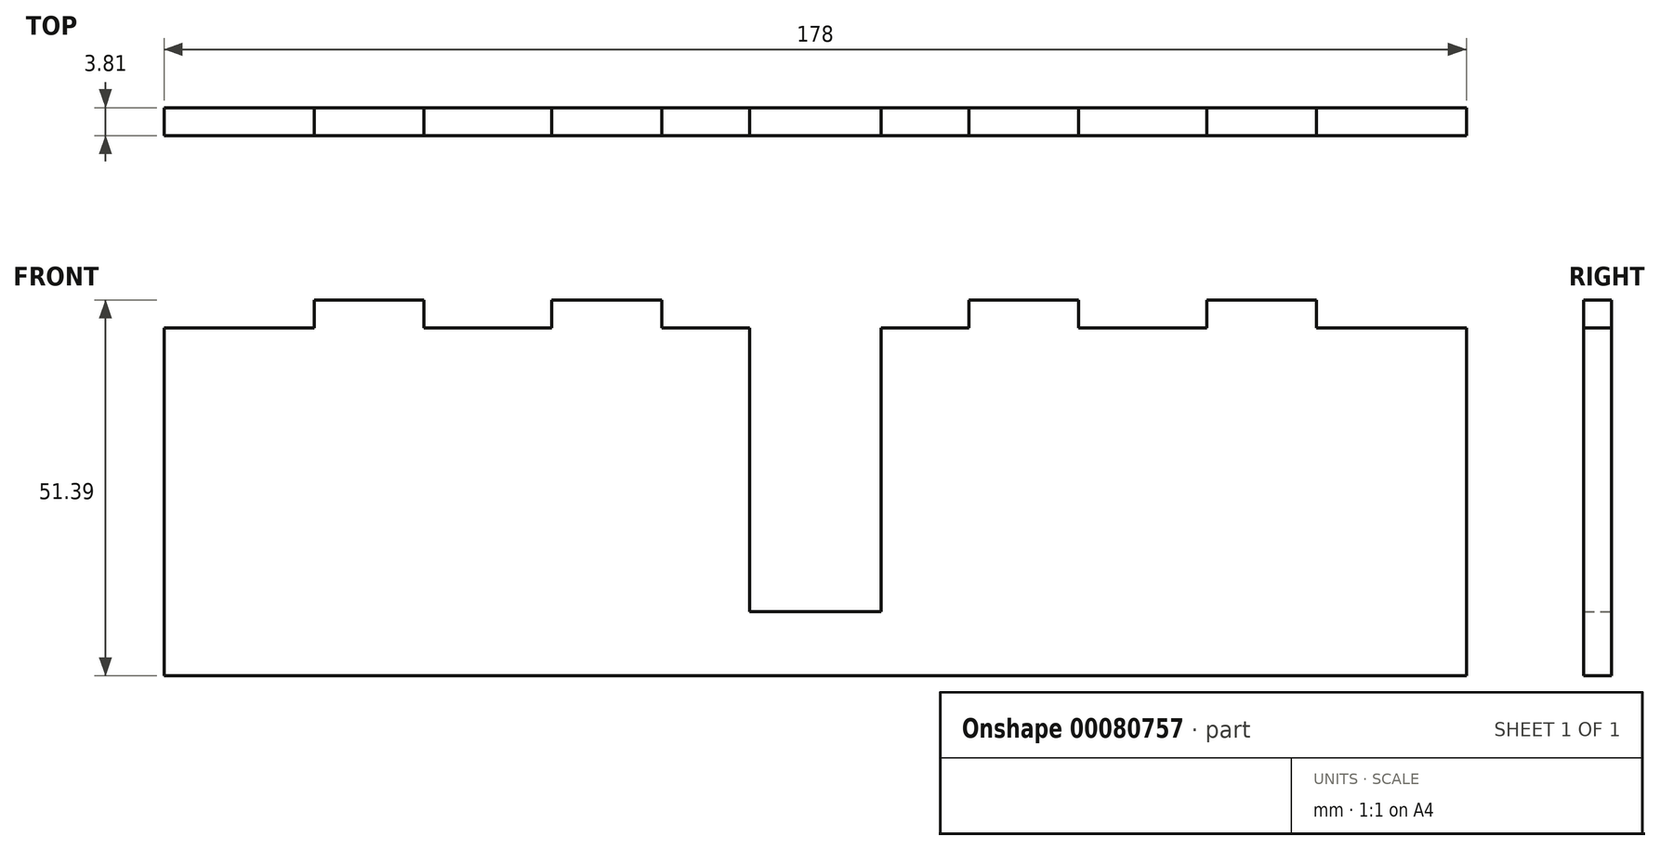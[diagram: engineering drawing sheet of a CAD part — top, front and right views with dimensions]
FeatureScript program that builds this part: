
annotation { "Feature Type Name" : "Feature", "Feature Type Description" : "" }
export const myFeature = defineFeature(function(context is Context, id is Id, definition is map)
    precondition{}
    {
        {
            var Q0;
            Q0=qCreatedBy(makeId("Front.planeOp"),FACE);
            var sketch = newSketch(context, id + "F0", { "sketchPlane" : qUnion([Q0])});
            skLineSegment(sketch, "E0.bottom", {"start": v(89, 23.79) * mm, "end": v(-89, 23.8) * mm});
            skLineSegment(sketch, "E0.top", {"start": v(89, -23.8) * mm, "end": v(-89, -23.79) * mm});
            skLineSegment(sketch, "E0.left", {"start": v(89, 23.79) * mm, "end": v(89, -23.79) * mm});
            skLineSegment(sketch, "E0.right", {"start": v(-89, 23.8) * mm, "end": v(-89, -23.79) * mm});
            skPoint(sketch, "E0.middle", {"position": v(0, 0) * mm});
            skLineSegment(sketch, "E1", {"start": v(0, 23.79) * mm, "end": v(0, -23.8) * mm});
            skLineSegment(sketch, "E2", {"start": v(-68.5, 23.79) * mm, "end": v(-68.5, 27.6) * mm});
            skLineSegment(sketch, "E3", {"start": v(-53.5, 23.79) * mm, "end": v(-53.5, 27.6) * mm});
            skLineSegment(sketch, "E4", {"start": v(-53.5, 27.6) * mm, "end": v(-68.5, 27.6) * mm});
            skLineSegment(sketch, "E5", {"start": v(-36, 23.79) * mm, "end": v(-36, 27.6) * mm});
            skLineSegment(sketch, "E6", {"start": v(-36, 27.6) * mm, "end": v(-21, 27.6) * mm});
            skLineSegment(sketch, "E7", {"start": v(-21, 27.6) * mm, "end": v(-21, 23.79) * mm});
            skLineSegment(sketch, "E8.MirrorCS", {"start": v(36, 27.6) * mm, "end": v(21, 27.6) * mm});
            skLineSegment(sketch, "E9.MirrorCS", {"start": v(36, 23.79) * mm, "end": v(36, 27.6) * mm});
            skLineSegment(sketch, "E10.MirrorCS", {"start": v(21, 27.6) * mm, "end": v(21, 23.79) * mm});
            skLineSegment(sketch, "E11.MirrorCS", {"start": v(53.5, 27.6) * mm, "end": v(68.5, 27.6) * mm});
            skLineSegment(sketch, "E12.MirrorCS", {"start": v(68.5, 23.8) * mm, "end": v(68.5, 27.6) * mm});
            skLineSegment(sketch, "E13.MirrorCS", {"start": v(53.5, 23.79) * mm, "end": v(53.5, 27.6) * mm});
            skLineSegment(sketch, "E14", {"start": v(-9, 23.79) * mm, "end": v(-9, 0) * mm});
            skLineSegment(sketch, "E15", {"start": v(-9, 0) * mm, "end": v(0, 0) * mm});
            skLineSegment(sketch, "E16.MirrorCS", {"start": v(9, 23.79) * mm, "end": v(9, 0) * mm});
            skLineSegment(sketch, "E17.MirrorCS", {"start": v(9, 0) * mm, "end": v(0, 0) * mm});
            skLineSegment(sketch, "E18", {"start": v(-9, 0) * mm, "end": v(-9, -15) * mm});
            skLineSegment(sketch, "E19", {"start": v(-9, -15) * mm, "end": v(9, -15) * mm});
            skLineSegment(sketch, "E20", {"start": v(9, -15) * mm, "end": v(9, 0) * mm});
            skSolve(sketch);
        }
        {
            var Q0;
            Q0=makeQuery(id+"F0.imprint","IMPRINT",FACE,{"disambiguationData":[TD([[makeQuery(id+"F0.imprint","IMPRINT",EDGE,{"derivedFrom":sQuery(id+"F0.wireOp",EDGE,"E0.bottom")}),1.0]])]});
            var Q1;
            {var subQ0=sQuery(id+"F0.wireOp",EDGE,"E2");Q1=makeQuery(id+"F0.imprint","IMPRINT",FACE,{"disambiguationData":[TD([[makeQuery(id+"F0.imprint","IMPRINT",EDGE,{"derivedFrom":subQ0}),-1.0]])]});}
            var Q2;
            {var subQ0=sQuery(id+"F0.wireOp",EDGE,"E5");Q2=makeQuery(id+"F0.imprint","IMPRINT",FACE,{"disambiguationData":[TD([[makeQuery(id+"F0.imprint","IMPRINT",EDGE,{"derivedFrom":subQ0}),-1.0]])]});}
            var Q3;
            Q3=makeQuery(id+"F0.imprint","IMPRINT",FACE,{"disambiguationData":[TD([[makeQuery(id+"F0.imprint","IMPRINT",EDGE,{"derivedFrom":sQuery(id+"F0.wireOp",EDGE,"E8.MirrorCS")}),1.0]])]});
            var Q4;
            Q4=makeQuery(id+"F0.imprint","IMPRINT",FACE,{"disambiguationData":[TD([[makeQuery(id+"F0.imprint","IMPRINT",EDGE,{"derivedFrom":sQuery(id+"F0.wireOp",EDGE,"E11.MirrorCS")}),-1.0]])]});
            extrude(context, id + "F1", {"entities" : qUnion([Q0, Q1, Q2, Q3, Q4]), "depth" : 3.8 * mm});
        }
    });
